# Revit family: IEK_Розетка_ОУ_З_16А_1-мест_IP54_FORS
name_source: partatom
category: Электрические приборы
units: mm (PartAtom-declared; Revit-internal decimal feet)

## family parameters
Всегда вертикально = Да
На основе рабочей плоскости = Нет
Общий = Нет
При загрузке вырезать с полостями = Нет
Размер круглого соединителя = Использовать диаметр
Сохранять ориентацию аннотаций = Да
Тип детали = Нормальный
Точка расчета площади = Нет

## types (2) — shared parameters
ADSK_URL страницы изделия = https://qr.iek.group
ADSK_Версия Revit = v2019
ADSK_Версия семейства = 01.10.25
ADSK_Группирование = Электроустановочные изделия низковольтные
ADSK_Единица измерения = шт.
ADSK_Завод-изготовитель = IEK
ADSK_Количество фаз = 1
ADSK_Количество фаз числовое = 1
ADSK_Марка = FORS
ADSK_Масса = 0.128
ADSK_Материал наименование = Пластик
ADSK_Напряжение = 220 В
URL = https://www.iek.ru
Высота = 92 мм
Глубина = 55 мм
Изготовитель = IEK
Описание = Электроустановочные изделия серии FORS подходят для эксплуатации в различных сферах, включая промышленные объекты, склады и производственные помещения. Благодаря степени защиты IP54 они стабильно работают в условиях повышенной влажности и запыленности. В комплекте есть подробная инструкция и необходимые аксессуары для быстрого монтажа. Электроустановочные изделия FORS — выбор профессионалов!
Степень защиты IP = IP54
Тип монтажа = Поверхность монтажа (открытая установка)
Ширина = 65 мм

## per-type parameters (varying)
| type | ADSK_Код изделия | ADSK_Материал | ADSK_Наименование | ADSK_Наименование краткое | Материал крышки |
| РСб20-3-ФСр_Серый | ERS12-K03-16-54-DC | Окраска - RAL 7035 | Розетка 1-местная с заземлением для открытой установки 16А IP54 РСб20-3-ФСр серый IEK | РСб20-3-ФСр | RAL 9004 |
| РСб20-3-ФБ_Белый | ERS12-K01-16-54-DC | Окраска - Белый | Розетка 1-местная с заземлением для открытой установки 16А IP54 РСб20-3-ФБ белый IEK | РСб20-3-ФБ | Окраска - Белый |
